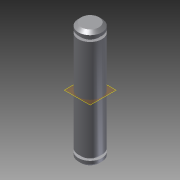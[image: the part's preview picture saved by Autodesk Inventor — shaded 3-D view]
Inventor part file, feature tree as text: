
AUTODESK INVENTOR PART (.ipt)
format: ipt  version: 2011 (Build 150229000, 229)  size: 94,720 bytes
history: native  units: mm (DEFAULTED — no unit token found)
features: revolve x1, sketch x1
ambient origin geometry x8: Origin, YZ Plane, XZ Plane, XY Plane, X Axis, Y Axis, Z Axis, Center Point
feature tree (2):
  revolve  "Revolution1"  [1 undecoded]
  sketch  "Sketch1"  dims[d4=35.0mm d5=1.0mm d6=36.0mm d7=2.0mm d19=90.0deg]
note: 1 required parameter value undecoded (feature->parameter linkage not recoverable at this tier; creation-order binding heuristic only, values carry confidence <= 0.55)
